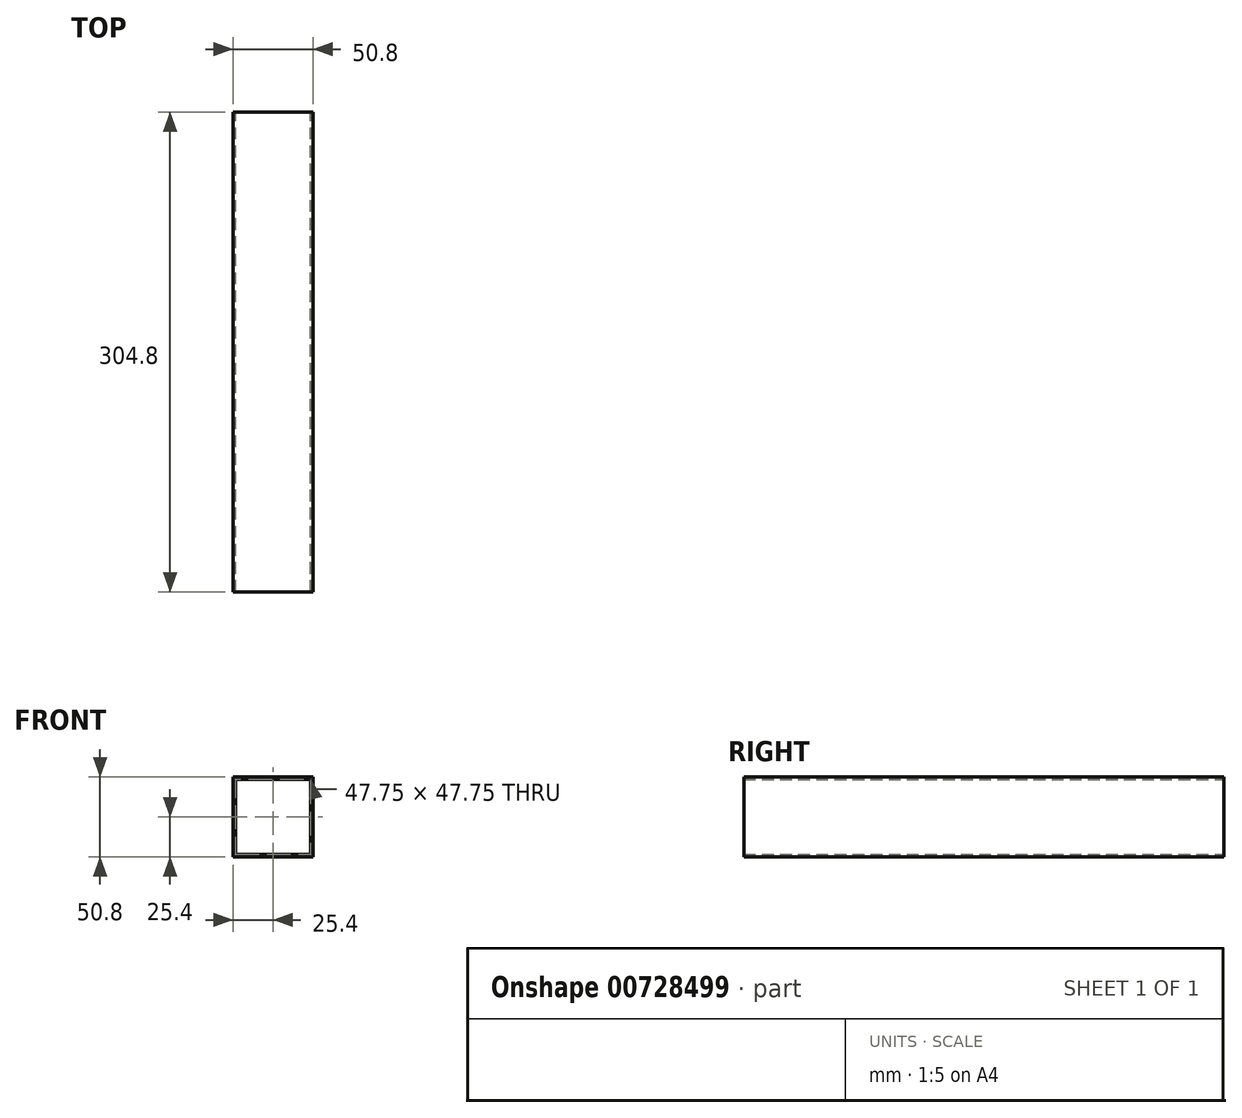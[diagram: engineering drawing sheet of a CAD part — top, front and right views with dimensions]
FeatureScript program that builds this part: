
annotation { "Feature Type Name" : "Feature", "Feature Type Description" : "" }
export const myFeature = defineFeature(function(context is Context, id is Id, definition is map)
    precondition{}
    {
        {
            var Q0;
            Q0=qCreatedBy(makeId("Front.planeOp"),FACE);
            var sketch = newSketch(context, id + "F0", { "sketchPlane" : qUnion([Q0])});
            skLineSegment(sketch, "E0.bottom", {"start": v(-25.4, 25.4) * mm, "end": v(25.4, 25.4) * mm});
            skLineSegment(sketch, "E0.top", {"start": v(-25.4, -25.4) * mm, "end": v(25.4, -25.4) * mm});
            skLineSegment(sketch, "E0.left", {"start": v(-25.4, 25.4) * mm, "end": v(-25.4, -25.4) * mm});
            skLineSegment(sketch, "E0.right", {"start": v(25.4, 25.4) * mm, "end": v(25.4, -25.4) * mm});
            skPoint(sketch, "E0.middle", {"position": v(0, 0) * mm});
            skLineSegment(sketch, "E1.bottom", {"start": v(-23.88, 23.88) * mm, "end": v(23.88, 23.88) * mm});
            skLineSegment(sketch, "E1.top", {"start": v(-23.88, -23.88) * mm, "end": v(23.88, -23.88) * mm});
            skLineSegment(sketch, "E1.left", {"start": v(-23.88, 23.88) * mm, "end": v(-23.88, -23.88) * mm});
            skLineSegment(sketch, "E1.right", {"start": v(23.88, 23.88) * mm, "end": v(23.88, -23.88) * mm});
            skSolve(sketch);
        }
        {
            var Q0;
            Q0=makeQuery(id+"F0.imprint","IMPRINT",FACE,{"disambiguationData":[TD([[makeQuery(id+"F0.imprint","IMPRINT",EDGE,{"derivedFrom":sQuery(id+"F0.wireOp",EDGE,"E0.bottom")}),-1.0]])]});
            extrude(context, id + "F1", {"entities" : qUnion([Q0]), "endBound" : BoundingType.SYMMETRIC, "depth" : 304.8 * mm, "offsetDistance" : 25.4 * mm});
        }
    });
